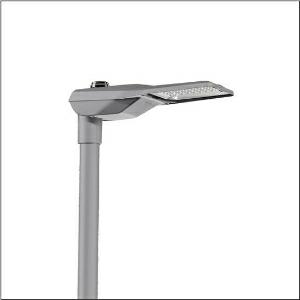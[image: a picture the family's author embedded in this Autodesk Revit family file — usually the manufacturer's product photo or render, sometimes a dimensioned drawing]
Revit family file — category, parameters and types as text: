
# Revit family: streetlight_sl_21_mini___p0_8a_5xe6u27n08hb_f017
name_source: partatom
category: Lighting Fixtures
units: mm (PartAtom-declared; Revit-internal decimal feet)

## family parameters
Cut with Voids When Loaded = No
Host = Face
Light Source = No
Part Type = Normal
Room Calculation Point = No
Round Connector Dimension = Use Diameter
Shared = No

## types (1)
- --- (1 x LED, 7550 lm, 66 W, 2200K)
    Apparent Load = 66 VA
    CIE Flux Codes = 33 69 96 100 100
    Color Rendering = 70
    Color Temperature = 2200K
    Default Elevation = 1800 mm
    Description = Streetlight SL 21 mini, mast luminaire, primary light control with lens, of PMMA, primary optical cover: cover, of toughened safety glass, transparent, light distribution: P0.8a, light emission: direct distribution, primary light characteristic: asymmetric, installation type: side-entry, LED, 3G 1.5mm², High Power LED, rated luminous flux: 7.550lm, luminous efficacy: 114lm/W, light colour: 722, colour temperature: 2200K, control gear: NEMA (7pin), control: flexible luminous flux parameterisation, time-dependent luminous flux control, constant luminous flux control, pre-setting: linear dimming characteristic, overheat protection, mains connection: 230..240V, AC, 50/60Hz, connection cable pre-assembled, cable length: 8,5m, wiring characteristics: H07RN-F, start of lifetime: 66W, end of service life: 69W, reduction: 30W, luminaire housing, of diecast aluminium (EN AC-44300), powder-coated, SITECO metallic grey (DB 702S), corrosivity category C5 high according to DIN EN ISO 12944, multi-level sealing system, sealing non-destructively replaceable, inclination adjustable: 0°, 5°, 10°, 15°, length: 628mm, width: 235mm, height: 110mm, spigot size: 42mm (side-entry), mounting height: 4..8m, protection rating (complete): IP66, insulation class (complete): insulation class I (protective earthing), certification: CE, ENEC, ENEC+, VDE, impact resistance: IK10, permissible operating ambient temperature for outdoor applications: -40..+50°C, standard-compliant lighting for roads and squares, packaging unit: 1 piece

Light Distribution: P0.8a
    Height = 110 mm
    Lamp = 1 x LED
    Lamp Light Flux = 7550 lm
    Lamp Power = 66 W
    Lamp count = 1
    Length = 625 mm
    Luminous efficacy = 114 lm/W
    Manufacturer = Siteco
    ModVariant = No
    Model = 5XE6U27N08HB
    Number of Poles = 1
    OnlyDefault = Yes
    Power Factor = 1
    Product Name = Streetlight SL 21 mini | P0.8a
    Product group = mast luminaire | pylon top
    ProductGroupID = 6100
    Protection Class = Protection class I
    Protection Degree = IP 66
    RLX_Detail_Level = 1
    RLX_Emergency_Light_Flux = 0 lm
    RLX_Emergency_Type = 0
    RLX_Emergency_Type_DB = No
    RlxData = <blob elided: 91861 chars, md5=614b22da>
    Socket = socket
    Standby Power = 0 W
    System Light Flux = 7550 lm
    System Power = 66 W
    Type Comments = factory setting: luminous flux: 100 % | dim-lin: 254 | 670 mA
    Type Image = l_1294379.jpg
    URL = http://relux.com
    VarID = @adj_081323
    Voltage = 0 V
    Weight = 0.00 kg
    Width = 234 mm

## geometry (parser evidence)
native form markers: Blend x4, Sweep x12
no freeform markers — native parametric forms only
